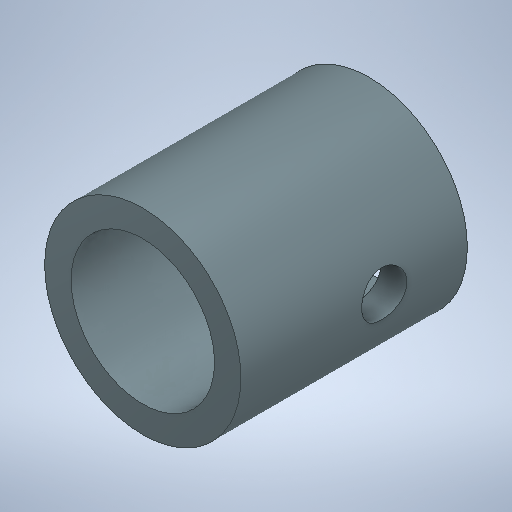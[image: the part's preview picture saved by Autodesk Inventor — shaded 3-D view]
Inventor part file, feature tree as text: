
AUTODESK INVENTOR PART (.ipt)
format: ipt  version: 2025.1 (Build 291241000, 241)  size: 246,272 bytes
history: native  units: mm
features: sketch x2, extrude x1, plane x1, hole x1
ambient origin geometry x8: Origin, YZ Plane, XZ Plane, XY Plane, X Axis, Y Axis, Z Axis, Center Point
bodies: Volumenkörper1 (feature_tree)
feature tree (5):
  extrude  "Extrusion1"  Depth=9.5mm
  plane  "Arbeitsebene1"
  hole  "Bohrung1"  [1 undecoded]
  sketch  "Skizze1"  dims[d0=13.0mm d1=9.5mm]
  sketch  "Skizze2"  dims[d2=15.0mm d3=0.0mm d4=6.5mm d5=9.5mm d6=3.0mm d7=6.0mm d8=4.0mm d9=2.0mm d10=90.0deg d11=3.0mm d12=0.0mm]
note: 1 required parameter value undecoded (feature->parameter linkage not recoverable at this tier; creation-order binding heuristic only, values carry confidence <= 0.55)
